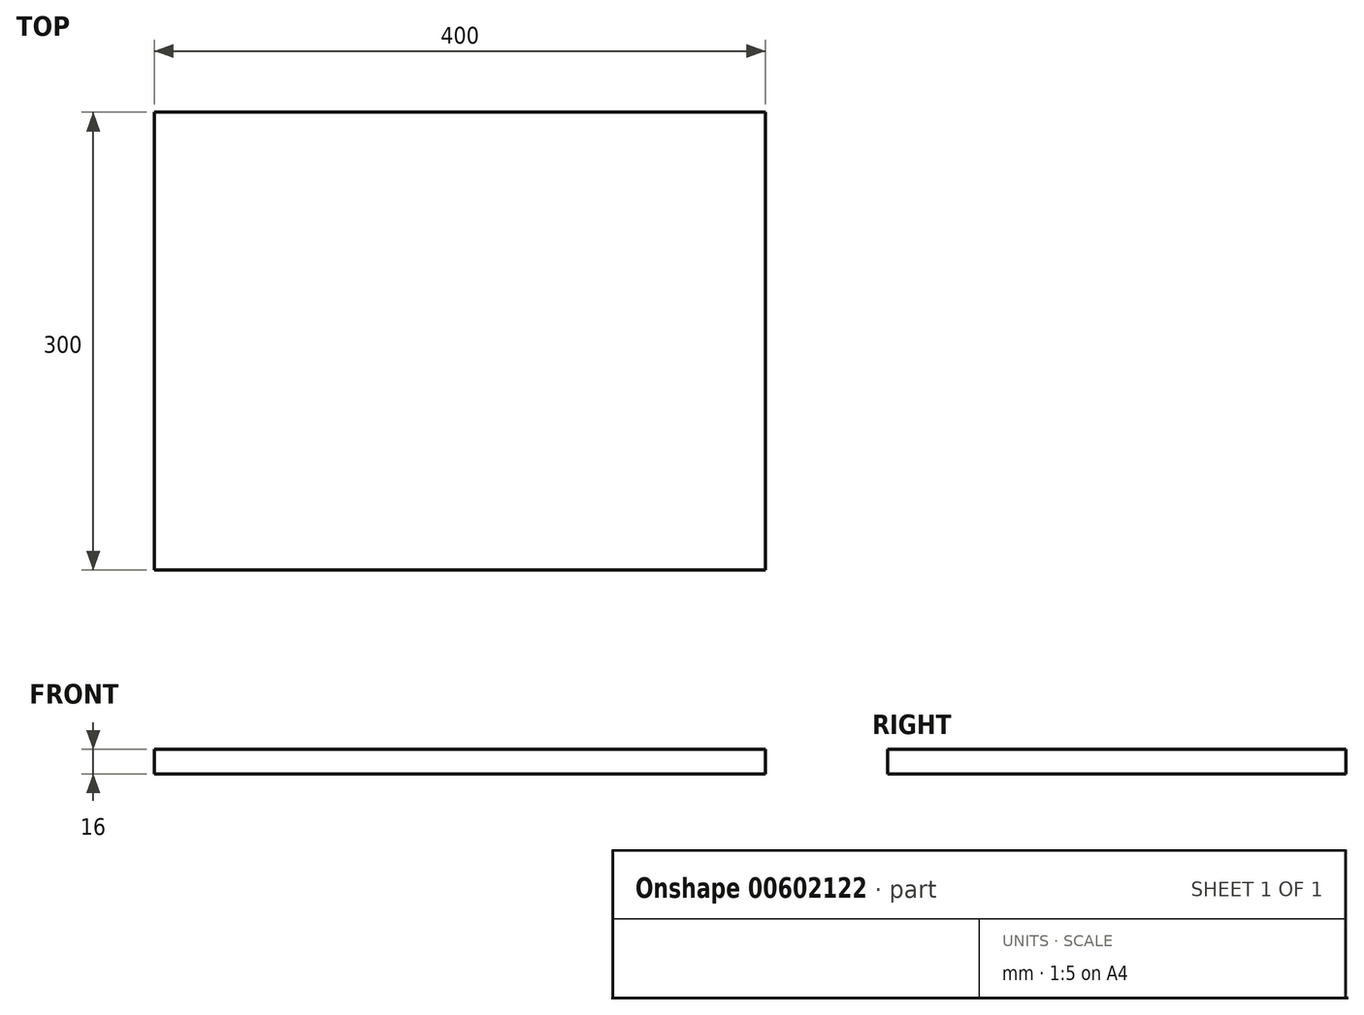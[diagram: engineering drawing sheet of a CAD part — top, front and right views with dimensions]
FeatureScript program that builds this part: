
annotation { "Feature Type Name" : "Feature", "Feature Type Description" : "" }
export const myFeature = defineFeature(function(context is Context, id is Id, definition is map)
    precondition{}
    {
        {
            var Q0;
            Q0=qCreatedBy(makeId("Top.planeOp"),FACE);
            var sketch = newSketch(context, id + "F0", { "sketchPlane" : qUnion([Q0])});
            skLineSegment(sketch, "E0.bottom", {"start": v(0, 0) * mm, "end": v(400, 0) * mm});
            skLineSegment(sketch, "E0.top", {"start": v(0, -300) * mm, "end": v(400, -300) * mm});
            skLineSegment(sketch, "E0.left", {"start": v(0, 0) * mm, "end": v(0, -300) * mm});
            skLineSegment(sketch, "E0.right", {"start": v(400, 0) * mm, "end": v(400, -300) * mm});
            skSolve(sketch);
        }
        {
            var Q0;
            Q0 = qSketchRegion(id + "F0", true);
            extrude(context, id + "F1", {"entities" : qUnion([Q0]), "depth" : 16 * mm, "offsetDistance" : 25 * mm});
        }
    });
